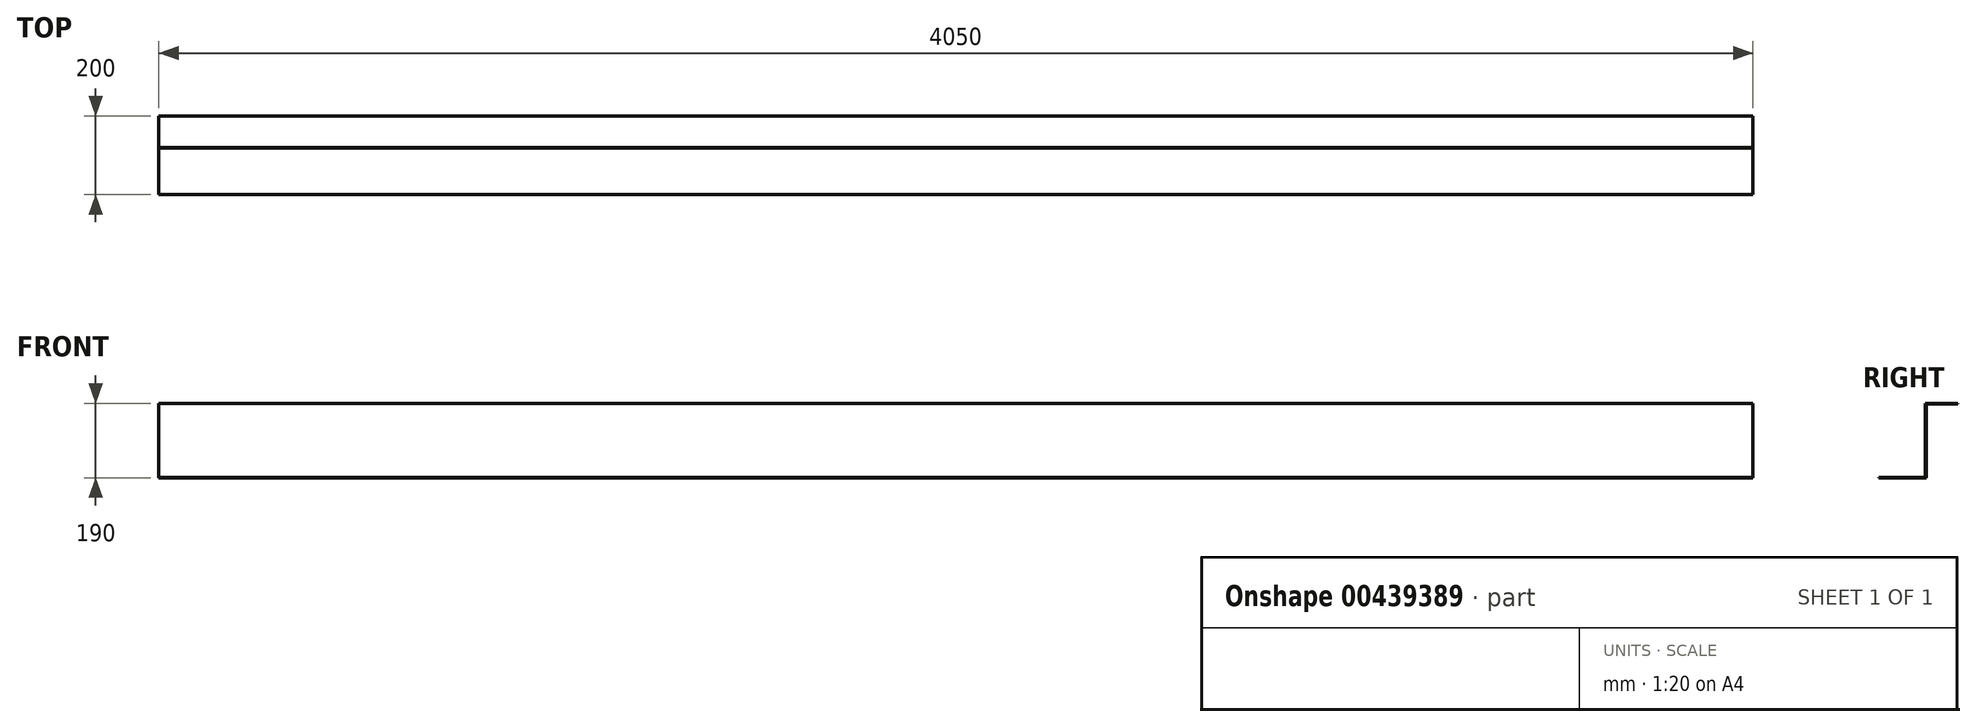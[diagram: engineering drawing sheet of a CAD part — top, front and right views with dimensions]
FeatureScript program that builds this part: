
annotation { "Feature Type Name" : "Feature", "Feature Type Description" : "" }
export const myFeature = defineFeature(function(context is Context, id is Id, definition is map)
    precondition{}
    {
        {
            var Q0;
            Q0=qCreatedBy(makeId("Top.planeOp"),FACE);
            var sketch = newSketch(context, id + "F0", { "sketchPlane" : qUnion([Q0])});
            skLineSegment(sketch, "E0.bottom", {"start": v(-109.18, 64.46) * mm, "end": v(3940.82, 64.46) * mm});
            skLineSegment(sketch, "E0.top", {"start": v(-109.18, -55.54) * mm, "end": v(3940.82, -55.54) * mm});
            skLineSegment(sketch, "E0.left", {"start": v(-109.18, 64.46) * mm, "end": v(-109.18, -55.54) * mm});
            skLineSegment(sketch, "E0.right", {"start": v(3940.82, 64.46) * mm, "end": v(3940.82, -55.54) * mm});
            skLineSegment(sketch, "E1.top", {"start": v(-109.18, 62.46) * mm, "end": v(3940.82, 62.46) * mm});
            skLineSegment(sketch, "E1.left", {"start": v(-109.18, 64.46) * mm, "end": v(-109.18, 62.46) * mm});
            skLineSegment(sketch, "E1.right", {"start": v(3940.82, 64.46) * mm, "end": v(3940.82, 62.46) * mm});
            skLineSegment(sketch, "E2.top", {"start": v(-109.18, 144.46) * mm, "end": v(3940.82, 144.46) * mm});
            skLineSegment(sketch, "E2.left", {"start": v(-109.18, 64.46) * mm, "end": v(-109.18, 144.46) * mm});
            skSolve(sketch);
        }
        {
            var Q0;
            {var subQ0=sQuery(id+"F0.wireOp",EDGE,"E0.top");Q0=makeQuery(id+"F0.imprint","IMPRINT",FACE,{"disambiguationData":[TD([[makeQuery(id+"F0.imprint","IMPRINT",EDGE,{"derivedFrom":subQ0}),1.0]])]});}
            extrude(context, id + "F1", {"entities" : qUnion([Q0]), "depth" : 2 * mm, "offsetDistance" : 25 * mm});
        }
        {
            var Q0;
            {var subQ0=sQuery(id+"F0.wireOp",EDGE,"E0.bottom");Q0=makeQuery(id+"F0.imprint","IMPRINT",FACE,{"disambiguationData":[TD([[makeQuery(id+"F0.imprint","IMPRINT",EDGE,{"derivedFrom":subQ0}),-1.0]])]});}
            extrude(context, id + "F2", {"entities" : qUnion([Q0]), "depth" : 190 * mm, "offsetDistance" : 25 * mm});
        }
        {
            var Q0;
            Q0=makeQuery(id+"F2.opExtrude","CAP_FACE",FACE,{"disambiguationData":[OSD([sQuery(id+"F0.wireOp",EDGE,"E0.bottom"),sQuery(id+"F0.wireOp",EDGE,"E0.left"),sQuery(id+"F0.wireOp",EDGE,"E0.right"),sQuery(id+"F0.wireOp",EDGE,"E1.top")])],"isStart":false});
            var sketch = newSketch(context, id + "F3", { "sketchPlane" : qUnion([Q0])});
            skLineSegment(sketch, "E3.bottom", {"start": v(-109.18, 64.46) * mm, "end": v(3940.82, 64.46) * mm});
            skLineSegment(sketch, "E3.top", {"start": v(-109.18, 144.46) * mm, "end": v(3940.82, 144.46) * mm});
            skLineSegment(sketch, "E3.left", {"start": v(-109.18, 64.46) * mm, "end": v(-109.18, 144.46) * mm});
            skLineSegment(sketch, "E3.right", {"start": v(3940.82, 64.46) * mm, "end": v(3940.82, 144.46) * mm});
            skSolve(sketch);
        }
        {
            var Q0;
            Q0=makeQuery(id+"F3.imprint","IMPRINT",FACE,{"disambiguationData":[TD([[makeQuery(id+"F3.imprint","IMPRINT",EDGE,{"derivedFrom":sQuery(id+"F3.wireOp",EDGE,"E3.bottom")}),1.0]])]});
            extrude(context, id + "F4", {"entities" : qUnion([Q0]), "oppositeDirection" : true, "depth" : 2 * mm, "offsetDistance" : 25 * mm});
        }
    });
